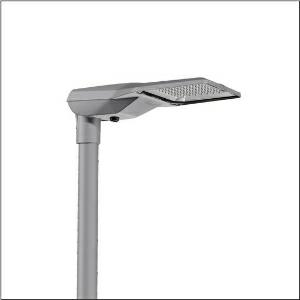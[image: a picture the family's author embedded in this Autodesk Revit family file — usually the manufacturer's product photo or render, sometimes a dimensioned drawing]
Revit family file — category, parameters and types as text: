
# Revit family: streetlight_sl_21_midi___st1_0ab_5xe3m33r08lb_2f09
name_source: partatom
category: Lighting Fixtures
units: mm (PartAtom-declared; Revit-internal decimal feet)

## family parameters
Cut with Voids When Loaded = No
Host = Face
Light Source = No
Part Type = Normal
Room Calculation Point = No
Round Connector Dimension = Use Diameter
Shared = No

## types (1)
- --- (1 x LED, 12620 lm, 99.6 W, 3000K)
    Apparent Load = 100 VA
    CIE Flux Codes = 38 73 97 100 100
    Color Rendering = 70
    Color Temperature = 3000K
    Default Elevation = 1800 mm
    Description = Streetlight SL 21 midi, mast luminaire, primary light control with lens, of PMMA, primary optical cover: cover, of toughened safety glass, transparent, light distribution: ST1.0aB, light emission: direct distribution, primary light characteristic: asymmetric, installation type: side-entry, post-top, LED, High Power LED, rated luminous flux: 12.620lm, luminous efficacy: 127lm/W, light colour: 730, colour temperature: 3000K, control gear: D4i, control: flexible luminous flux parameterisation, time-dependent luminous flux control, constant luminous flux control, overheat protection, pre-setting: logarithmic dimming characteristic, mains connection: 230..240V, AC, 50/60Hz, start of lifetime: 100W, end of service life: 102W, reduction: 46W, luminaire housing, of diecast aluminium, powder-coated, SITECO metallic grey (DB 702S), corrosivity category C5 high according to DIN EN ISO 12944, please order mast flange separately, inclination adjustable: 0°, 5°, 10°, 15°, sealing non-destructively replaceable, multi-level sealing system, length: 644mm, width: 335mm, height: 110mm, mast flange for spigot size: 42mm (side-entry): 5XC10008XM4, 60/48mm (side-entry/post-top): 5XC10108XM2, 76/60mm (side-entry/post-top): 5XC10108XM1, mounting height: 4..8m, Smart Interface below, protection rating (complete): IP66, insulation class (complete): insulation class II (safety insulation), certification: CE, ENEC, ENEC+, VDE, impact resistance: IK10, permissible operating ambient temperature for outdoor applications: -40..+50°C, standard-compliant lighting for roads and squares, packaging unit: 1 piece

Light Distribution: ST1.0aB
    Height = 111 mm
    Lamp = 1 x LED
    Lamp Light Flux = 12620 lm
    Lamp Power = 99.6 W
    Lamp count = 1
    Length = 644 mm
    Luminous efficacy = 127 lm/W
    Manufacturer = Siteco
    ModVariant = No
    Model = 5XE3M33R08LB
    Number of Poles = 1
    OnlyDefault = Yes
    Power Factor = 1
    Product Name = Streetlight SL 21 midi | ST1.0aB
    Product group = mast luminaire | pylon top
    ProductGroupID = 6100
    Protection Class = Protection class II
    Protection Degree = IP 66
    RLX_Detail_Level = 1
    RLX_Emergency_Light_Flux = 0 lm
    RLX_Emergency_Type = 0
    RLX_Emergency_Type_DB = No
    RlxData = <blob elided: 26953 chars, md5=4a5d1f6e>
    Socket = socket
    Standby Power = 0 W
    System Light Flux = 12620 lm
    System Power = 100 W
    Type Comments = factory setting: luminous flux: 100 % | dim-lin: 254 | 1020 mA
    Type Image = l_1004300.jpg
    URL = http://relux.com
    VarID = @adj_030665
    Voltage = 0 V
    Weight = 0.00 kg
    Width = 336 mm

## geometry (parser evidence)
native form markers: Blend x4, Sweep x11
no freeform markers — native parametric forms only
